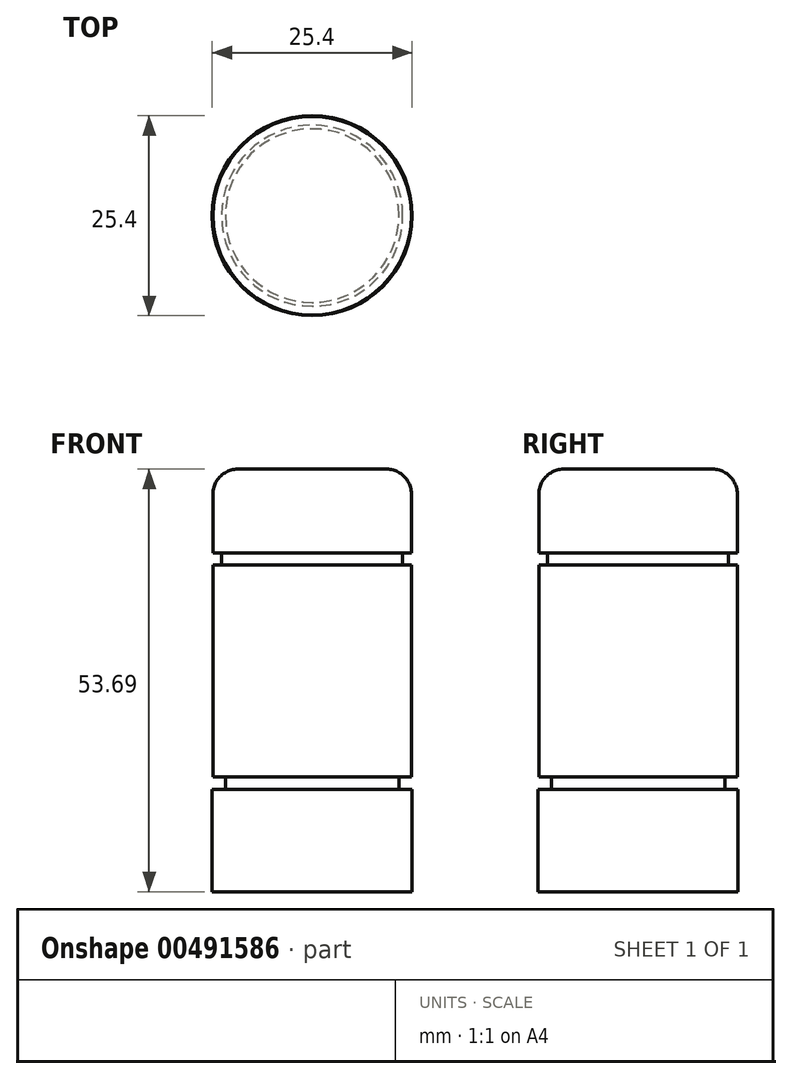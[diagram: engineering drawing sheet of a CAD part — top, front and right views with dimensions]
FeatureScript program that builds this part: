
annotation { "Feature Type Name" : "Feature", "Feature Type Description" : "" }
export const myFeature = defineFeature(function(context is Context, id is Id, definition is map)
    precondition{}
    {
        {
            var Q0;
            Q0=qCreatedBy(makeId("Front.planeOp"),FACE);
            var sketch = newSketch(context, id + "F0", { "sketchPlane" : qUnion([Q0])});
            skLineSegment(sketch, "E0.right", {"start": v(0, 25.58) * mm, "end": v(0, -28.1) * mm, "construction": true});
            skLineSegment(sketch, "E1", {"start": v(11.03, -13.53) * mm, "end": v(11.03, -15.1) * mm, "construction": true});
            skLineSegment(sketch, "E2", {"start": v(11.5, 14.96) * mm, "end": v(11.5, 13.39) * mm, "construction": true});
            skLineSegment(sketch, "E3", {"start": v(11.5, 13.39) * mm, "end": v(12.6, 13.39) * mm});
            skLineSegment(sketch, "E4", {"start": v(11.5, 14.96) * mm, "end": v(11.5, 13.39) * mm});
            skLineSegment(sketch, "E5", {"start": v(12.6, 13.39) * mm, "end": v(12.6, -13.53) * mm});
            skLineSegment(sketch, "E6", {"start": v(11.03, -13.53) * mm, "end": v(12.6, -13.53) * mm});
            skLineSegment(sketch, "E7", {"start": v(11.03, -13.53) * mm, "end": v(11.03, -15.1) * mm});
            skLineSegment(sketch, "E8", {"start": v(11.03, -15.1) * mm, "end": v(12.7, -15.1) * mm});
            skLineSegment(sketch, "E9", {"start": v(12.7, -15.1) * mm, "end": v(12.7, -28.1) * mm});
            skLineSegment(sketch, "E10", {"start": v(12.7, -28.1) * mm, "end": v(0, -28.1) * mm});
            skLineSegment(sketch, "E11", {"start": v(11.5, 14.96) * mm, "end": v(12.6, 14.96) * mm});
            skLineSegment(sketch, "E12", {"start": v(12.6, 14.96) * mm, "end": v(12.6, 22.44) * mm});
            skLineSegment(sketch, "E13", {"start": v(9.46, 25.58) * mm, "end": v(0, 25.58) * mm});
            skPoint(sketch, "E14.visualSharp", {"position": v(12.6, 25.58) * mm});
            skArc(sketch, "E14.filletArc", {"start": v(12.6, 22.44) * mm, "mid": v(11.68, 24.66) * mm, "end": v(9.46, 25.58) * mm});
            skLineSegment(sketch, "E15", {"start": v(0, 25.58) * mm, "end": v(0, -28.1) * mm});
            skSolve(sketch);
        }
        {
            var Q0;
            Q0 = qSketchRegion(id + "F0", true);
            var Q1;
            Q1=sQuery(id+"F0.wireOp",EDGE,"E15");
            revolve(context, id + "F1", {"entities" : qUnion([Q0]), "axis" : qUnion([Q1]), "revolveType" : RevolveType.FULL});
        }
    });
